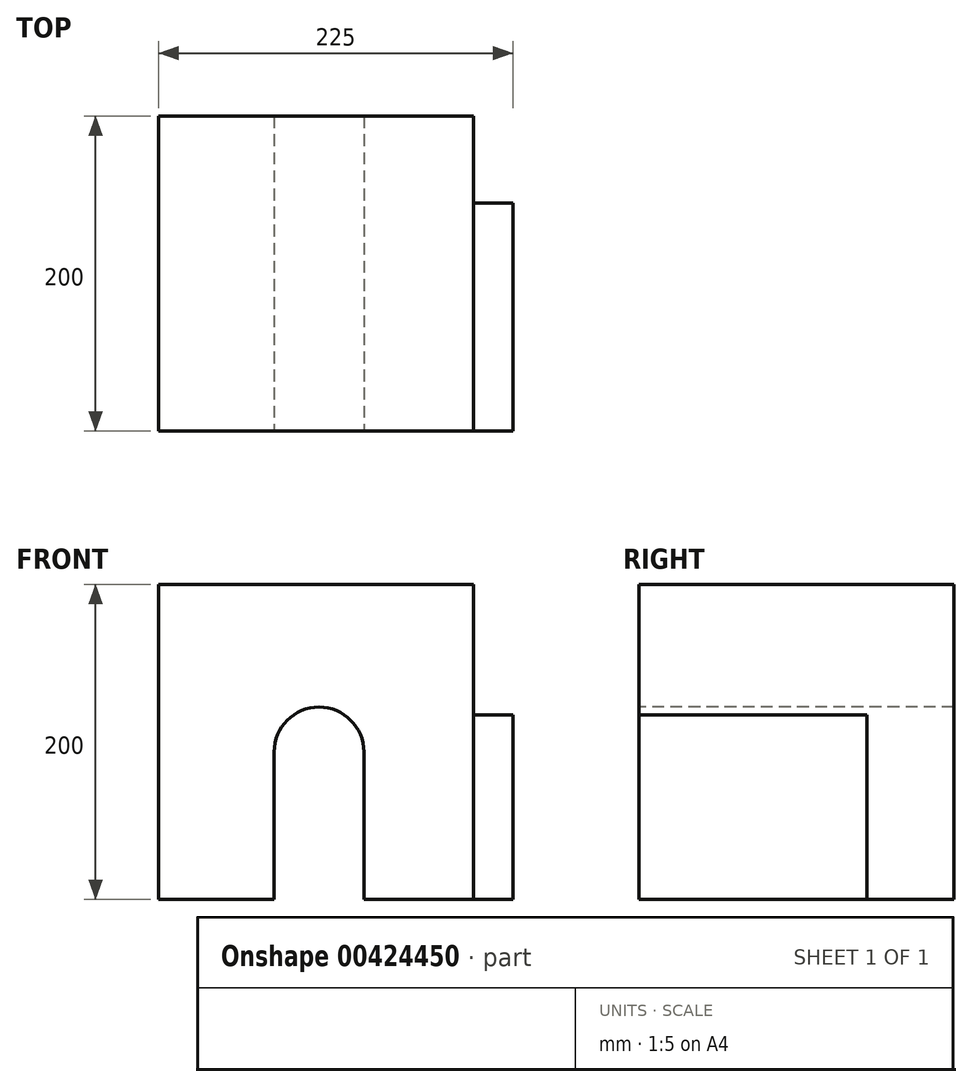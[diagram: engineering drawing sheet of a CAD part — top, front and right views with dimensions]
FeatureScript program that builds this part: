
annotation { "Feature Type Name" : "Feature", "Feature Type Description" : "" }
export const myFeature = defineFeature(function(context is Context, id is Id, definition is map)
    precondition{}
    {
        {
            var Q0;
            Q0=qCreatedBy(makeId("Front.planeOp"),FACE);
            var sketch = newSketch(context, id + "F0", { "sketchPlane" : qUnion([Q0])});
            skLineSegment(sketch, "E0.bottom", {"start": v(-43.77, 0) * mm, "end": v(156.23, 0) * mm});
            skLineSegment(sketch, "E0.top", {"start": v(-43.77, 200) * mm, "end": v(156.23, 200) * mm});
            skLineSegment(sketch, "E0.left", {"start": v(-43.77, 0) * mm, "end": v(-43.77, 200) * mm});
            skLineSegment(sketch, "E0.right", {"start": v(156.23, 0) * mm, "end": v(156.23, 200) * mm});
            skSolve(sketch);
        }
        {
            var Q0;
            Q0=makeQuery(id+"F0.imprint","IMPRINT",FACE,{"disambiguationData":[TD([[makeQuery(id+"F0.imprint","IMPRINT",EDGE,{"derivedFrom":sQuery(id+"F0.wireOp",EDGE,"E0.bottom")}),1.0]])]});
            extrude(context, id + "F1", {"entities" : qUnion([Q0]), "depth" : 200 * mm});
        }
        {
            var Q0;
            Q0=makeQuery(id+"F1.opExtrude","CAP_FACE",FACE,{"disambiguationData":[OSD([sQuery(id+"F0.wireOp",EDGE,"E0.bottom"),sQuery(id+"F0.wireOp",EDGE,"E0.top"),sQuery(id+"F0.wireOp",EDGE,"E0.left"),sQuery(id+"F0.wireOp",EDGE,"E0.right")])],"isStart":false});
            var sketch = newSketch(context, id + "F2", { "sketchPlane" : qUnion([Q0])});
            skLineSegment(sketch, "E1.bottom", {"start": v(29.58, 0) * mm, "end": v(86.54, 0) * mm});
            skLineSegment(sketch, "E1.left", {"start": v(29.58, 0) * mm, "end": v(29.58, 93.65) * mm});
            skLineSegment(sketch, "E1.right", {"start": v(86.54, 0) * mm, "end": v(86.54, 93.65) * mm});
            skArc(sketch, "E2", {"start": v(86.54, 93.65) * mm, "mid": v(58.06, 122.14) * mm, "end": v(29.58, 93.65) * mm});
            skSolve(sketch);
        }
        {
            var Q0;
            Q0=makeQuery(id+"F2.imprint","IMPRINT",FACE,{"disambiguationData":[TD([[makeQuery(id+"F2.imprint","IMPRINT",EDGE,{"derivedFrom":sQuery(id+"F2.wireOp",EDGE,"E1.bottom")}),1.0]])]});
            extrude(context, id + "F3", {"entities" : qUnion([Q0]), "operationType" : NewBodyOperationType.REMOVE, "endBound" : BoundingType.UP_TO_NEXT, "oppositeDirection" : true, "depth" : 25 * mm});
        }
        {
            var Q0;
            Q0=makeQuery(id+"F1.opExtrude","SWEPT_FACE",FACE,{"disambiguationData":[OSD([sQuery(id+"F0.wireOp",EDGE,"E0.right")])]});
            var sketch = newSketch(context, id + "F4", { "sketchPlane" : qUnion([Q0])});
            skLineSegment(sketch, "E3.bottom", {"start": v(-200, 117.3) * mm, "end": v(-55.15, 117.3) * mm});
            skLineSegment(sketch, "E3.top", {"start": v(-200, 0) * mm, "end": v(-55.15, 0) * mm});
            skLineSegment(sketch, "E3.left", {"start": v(-200, 117.3) * mm, "end": v(-200, 0) * mm});
            skLineSegment(sketch, "E3.right", {"start": v(-55.15, 117.3) * mm, "end": v(-55.15, 0) * mm});
            skSolve(sketch);
        }
        {
            var Q0;
            Q0=makeQuery(id+"F4.imprint","IMPRINT",FACE,{"disambiguationData":[TD([[makeQuery(id+"F4.imprint","IMPRINT",EDGE,{"derivedFrom":sQuery(id+"F4.wireOp",EDGE,"E3.bottom")}),-1.0]])]});
            extrude(context, id + "F5", {"entities" : qUnion([Q0]), "depth" : 25 * mm, "offsetDistance" : 25 * mm});
        }
    });
